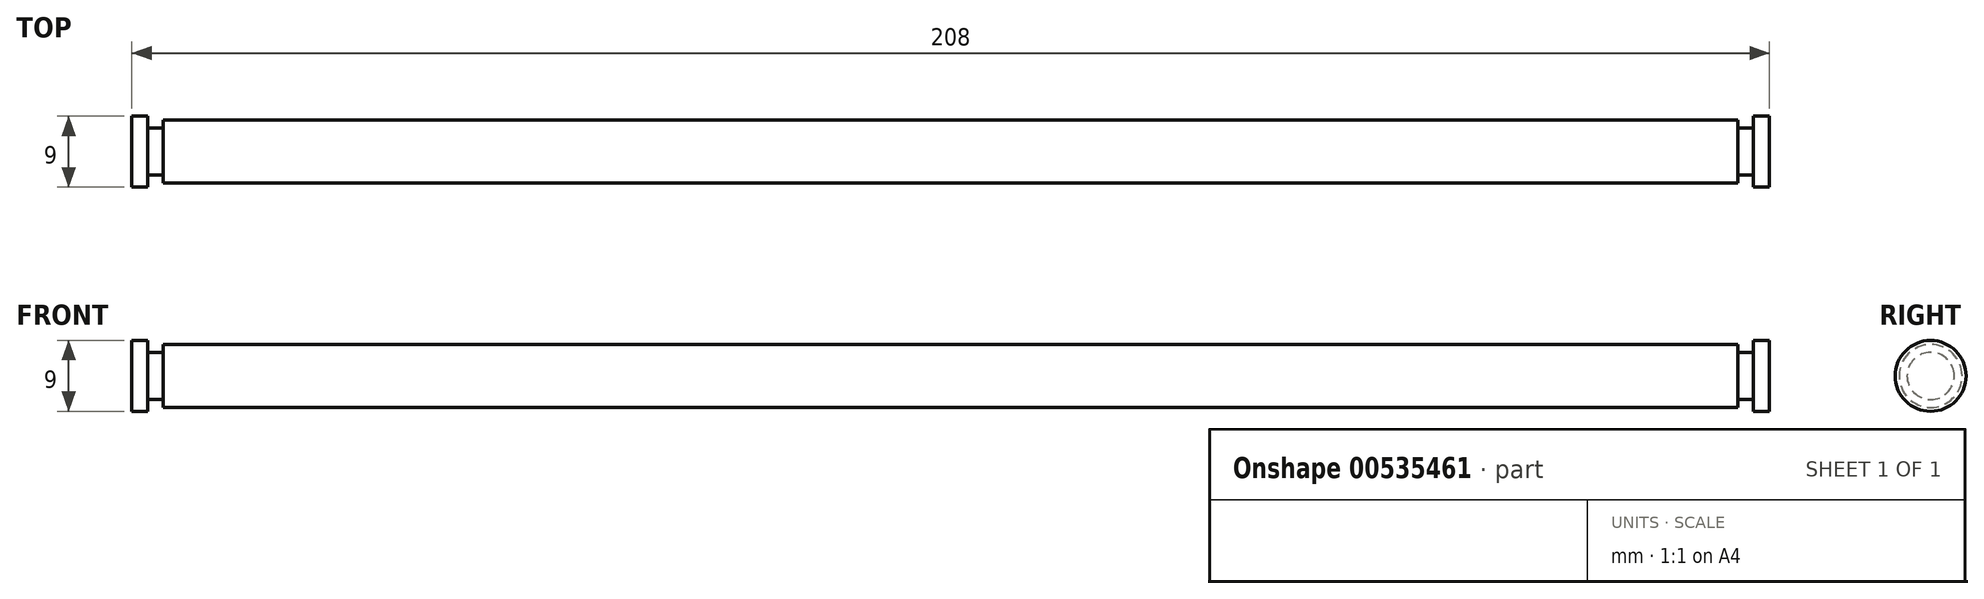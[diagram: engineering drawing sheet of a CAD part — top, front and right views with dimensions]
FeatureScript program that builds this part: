
annotation { "Feature Type Name" : "Feature", "Feature Type Description" : "" }
export const myFeature = defineFeature(function(context is Context, id is Id, definition is map)
    precondition{}
    {
        {
            var Q0;
            Q0=qCreatedBy(makeId("Right.planeOp"),FACE);
            var sketch = newSketch(context, id + "F0", { "sketchPlane" : qUnion([Q0])});
            skCircle(sketch, "E0", {"center": v(0, 0) * mm, "radius": 4 * mm});
            skSolve(sketch);
        }
        {
            var Q0;
            Q0=makeQuery(id+"F0.imprint","IMPRINT",FACE,{"disambiguationData":[TD([[makeQuery(id+"F0.imprint","IMPRINT",EDGE,{"derivedFrom":sQuery(id+"F0.wireOp",EDGE,"E0")}),1.0]])]});
            extrude(context, id + "F1", {"entities" : qUnion([Q0]), "depth" : 100 * mm, "offsetDistance" : 25 * mm});
        }
        {
            var Q0;
            Q0=makeQuery(id+"F1.opExtrude","CAP_FACE",FACE,{"disambiguationData":[OSD([sQuery(id+"F0.wireOp",EDGE,"E0")])],"isStart":false});
            var sketch = newSketch(context, id + "F2", { "sketchPlane" : qUnion([Q0])});
            skCircle(sketch, "E1", {"center": v(0, 0) * mm, "radius": 3 * mm});
            skSolve(sketch);
        }
        {
            var Q0;
            Q0=makeQuery(id+"F2.imprint","IMPRINT",FACE,{"disambiguationData":[TD([[makeQuery(id+"F2.imprint","IMPRINT",EDGE,{"derivedFrom":sQuery(id+"F2.wireOp",EDGE,"E1")}),1.0]])]});
            extrude(context, id + "F3", {"entities" : qUnion([Q0]), "operationType" : NewBodyOperationType.ADD, "depth" : 2 * mm, "offsetDistance" : 25 * mm});
        }
        {
            var Q0;
            Q0=makeQuery(id+"F3.opExtrude","CAP_FACE",FACE,{"disambiguationData":[OSD([sQuery(id+"F2.wireOp",EDGE,"E1")])],"isStart":false});
            var sketch = newSketch(context, id + "F4", { "sketchPlane" : qUnion([Q0])});
            skCircle(sketch, "E2", {"center": v(0, 0) * mm, "radius": 4.5 * mm});
            skSolve(sketch);
        }
        {
            var Q0;
            Q0=makeQuery(id+"F4.imprint","IMPRINT",FACE,{"disambiguationData":[TD([[makeQuery(id+"F4.imprint","IMPRINT",EDGE,{"derivedFrom":sQuery(id+"F4.wireOp",EDGE,"E2")}),1.0]])]});
            var Q1;
            Q1=makeQuery(id+"F4.imprint","IMPRINT",FACE,{"disambiguationData":[TD([[makeQuery(id+"F4.imprint","IMPRINT",EDGE,{"derivedFrom":makeQuery(id+"F3.opExtrude","CAP_EDGE",EDGE,{"disambiguationData":[OSD([sQuery(id+"F2.wireOp",EDGE,"E1")])],"isStart":false})}),1.0]])]});
            extrude(context, id + "F5", {"entities" : qUnion([Q0, Q1]), "operationType" : NewBodyOperationType.ADD, "depth" : 2 * mm, "offsetDistance" : 25 * mm});
        }
        {
            var Q0;
            Q0=makeQuery(id+"F1.opExtrude","SWEPT_BODY",BODY,{"disambiguationData":[OSD([sQuery(id+"F0.wireOp",EDGE,"E0")])]});
            var Q1;
            Q1=qCreatedBy(makeId("Right.planeOp"),FACE);
            mirror(context, id + "F6", {"operationType" : NewBodyOperationType.ADD, "entities" : qUnion([Q0]), "mirrorPlane" : qUnion([Q1])});
        }
    });
